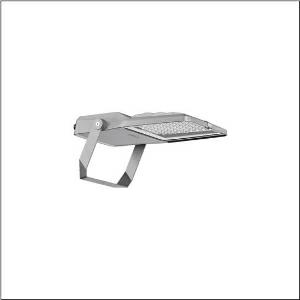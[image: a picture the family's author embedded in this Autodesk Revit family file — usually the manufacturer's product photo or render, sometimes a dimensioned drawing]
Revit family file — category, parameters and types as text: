
# Revit family: floodlight_fl_21_iq_mini___pl43_5xa7772d2a1a_725a
name_source: partatom
category: Lighting Fixtures
units: mm (PartAtom-declared; Revit-internal decimal feet)

## family parameters
Cut with Voids When Loaded = No
Host = Face
Light Source = No
Part Type = Normal
Room Calculation Point = No
Round Connector Dimension = Use Diameter
Shared = No

## types (1)
- --- (1 x LED, 18290 lm, 143 W, 3000K)
    Apparent Load = 143 VA
    CIE Flux Codes = 27 78 99 100 100
    Color Rendering = 70
    Color Temperature = 3000K
    Default Elevation = 1800 mm
    Description = Floodlight FL 21 iQ mini, floodlight, primary light control with lens, of PMMA, primary optical cover: protective disc, of toughened safety glass, transparent, light distribution: PL43, light emission: direct distribution, installation type: surface-mounted, LED, High Power LED, rated luminous flux: 18.290lm, luminous efficacy: 128lm/W, light colour: 730, colour temperature: 3000K, control gear: iQ Street-Remote/DALI, control: Street-Remote, Auto-Match, Temp-Guard, Night-Set, Smart-Wire, Desk-Remote (wireless, voltage-free reading and setting of iQ features in the workshop via application-optimized NFC function/RFID function), optimised constant luminous flux control (CLO 2.0), with terminal, 6-pole, mains connection: 220..240V, AC, 50/60Hz, start of lifetime: 143W, end of service life: 152W, reduction: 61W, luminaire housing, of diecast aluminium, powder-coated, Siteco® metallic grey (DB 702S), corrosivity category C5 mid according to DIN EN ISO 12944, suitable for swimming pools, chlorine-resistant, sealing non-destructively replaceable, mounting bracket, of steel, galvanised, powder-coated, Siteco® metallic grey (DB 702S), protection rating (complete): IP66, insulation class (complete): insulation class II (safety insulation), certification: CE, ENEC, VDE, protection symbol: D, impact resistance: IK08, permissible operating ambient temperature: -40..+40°C, permissible operating ambient temperature for outdoor applications: -40..+50°C, standard: DIN EN 12944, LABS conformity tested according to VDMA 24364:2018-05, packaging unit: 1 piece

Light Distribution: PL43
    Height = 70 mm
    Lamp = 1 x LED
    Lamp Light Flux = 18290 lm
    Lamp Power = 143 W
    Lamp count = 1
    Length = 485 mm
    Luminous efficacy = 128 lm/W
    Manufacturer = Siteco
    ModVariant = No
    Model = 5XA7772D2A1A
    Number of Poles = 1
    OnlyDefault = Yes
    Power Factor = 1
    Product Name = Floodlight FL 21 iQ mini | PL43
    Product group = floodlight | pylon annexe
    ProductGroupID = 6200
    Protection Class = Protection class II
    Protection Degree = IP 66
    RLX_Detail_Level = 1
    RLX_Emergency_Light_Flux = 0 lm
    RLX_Emergency_Type = 0
    RLX_Emergency_Type_DB = No
    RlxData = <blob elided: 96497 chars, md5=f1e21609>
    Socket = socket
    Standby Power = 0 W
    System Light Flux = 18290 lm
    System Power = 143 W
    Type Comments = factory setting: luminous flux: 100 % | dim-lin: 254 | 730 mA
    Type Image = l_1006845.jpg
    URL = http://relux.com
    VarID = @adj_162050
    Voltage = 0 V
    Weight = 0.00 kg
    Width = 337 mm

## geometry (parser evidence)
native form markers: Blend x4, Sweep x14
no freeform markers — native parametric forms only
